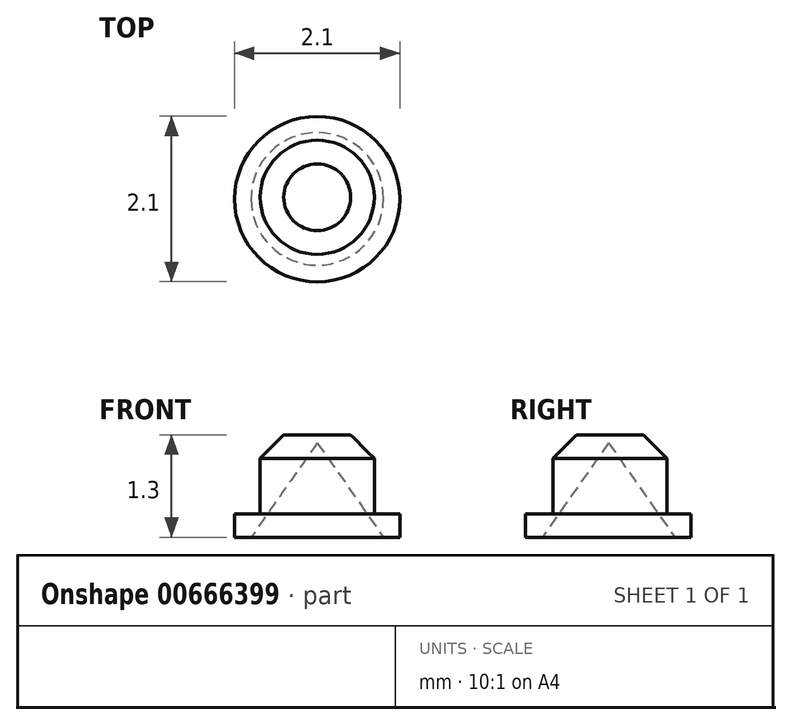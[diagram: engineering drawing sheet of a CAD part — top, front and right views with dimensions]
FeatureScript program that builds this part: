
annotation { "Feature Type Name" : "Feature", "Feature Type Description" : "" }
export const myFeature = defineFeature(function(context is Context, id is Id, definition is map)
    precondition{}
    {
        {
            var Q0;
            Q0=qCreatedBy(makeId("Top.planeOp"),FACE);
            var sketch = newSketch(context, id + "F0", { "sketchPlane" : qUnion([Q0])});
            skCircle(sketch, "E0", {"center": v(0, 0) * mm, "radius": 0.73 * mm});
            skSolve(sketch);
        }
        {
            var Q0;
            Q0=makeQuery(id+"F0.imprint","IMPRINT",FACE,{"disambiguationData":[TD([[makeQuery(id+"F0.imprint","IMPRINT",EDGE,{"derivedFrom":sQuery(id+"F0.wireOp",EDGE,"E0")}),1.0]])]});
            extrude(context, id + "F1", {"entities" : qUnion([Q0]), "flatOperationType" : FlatOperationType.REMOVE, "thickness1" : 5 * mm, "thickness2" : 0 * mm, "thickness" : 5 * mm, "depth" : 1 * mm, "offsetDistance" : 25 * mm, "startOffsetBound" : StartOffsetType.BLIND, "startOffsetDistance" : 25 * mm, "domain" : OperationDomain.MODEL});
        }
        {
            var Q0;
            Q0=makeQuery(id+"F1.opExtrude","CAP_FACE",FACE,{"disambiguationData":[OSD([sQuery(id+"F0.wireOp",EDGE,"E0")])],"isStart":true});
            var sketch = newSketch(context, id + "F2", { "sketchPlane" : qUnion([Q0])});
            skCircle(sketch, "E1", {"center": v(0, 0.02) * mm, "radius": 1.05 * mm});
            skSolve(sketch);
        }
        {
            var Q0;
            Q0=makeQuery(id+"F2.imprint","IMPRINT",FACE,{"disambiguationData":[TD([[makeQuery(id+"F2.imprint","IMPRINT",EDGE,{"derivedFrom":sQuery(id+"F2.wireOp",EDGE,"E1")}),1.0]])]});
            extrude(context, id + "F3", {"entities" : qUnion([Q0]), "operationType" : NewBodyOperationType.ADD, "depth" : -0.3 * mm, "offsetDistance" : 25 * mm});
        }
        {
            var Q0;
            Q0=makeQuery(id+"F1.opExtrude","CAP_FACE",FACE,{"disambiguationData":[OSD([sQuery(id+"F0.wireOp",EDGE,"E0")])],"isStart":false});
            extrude(context, id + "F4", {"entities" : qUnion([Q0]), "operationType" : NewBodyOperationType.ADD, "depth" : 0.3 * mm, "offsetDistance" : 25 * mm});
        }
        {
            var Q0;
            Q0=makeQuery(id+"F4.opExtrude","CAP_EDGE",EDGE,{"disambiguationData":[OSD([sQuery(id+"F0.wireOp",EDGE,"E0")])],"isStart":false});
            chamfer(context, id + "F5", {"entities" : qUnion([Q0]), "width" : 0.3 * mm, "tangentPropagation" : true});
        }
        {
            var Q0;
            Q0=qCreatedBy(makeId("Front.planeOp"),FACE);
            var sketch = newSketch(context, id + "F6", { "sketchPlane" : qUnion([Q0])});
            skLineSegment(sketch, "E2", {"start": v(0, 0) * mm, "end": v(0, -1.21) * mm});
            skLineSegment(sketch, "E3", {"start": v(0, -1.21) * mm, "end": v(-0.85, -1.21) * mm});
            skLineSegment(sketch, "E4", {"start": v(-0.85, -1.21) * mm, "end": v(0, 0) * mm});
            skSolve(sketch);
        }
        {
            var Q0;
            Q0=makeQuery(id+"F6.imprint","IMPRINT",FACE,{"disambiguationData":[TD([[makeQuery(id+"F6.imprint","IMPRINT",EDGE,{"derivedFrom":sQuery(id+"F6.wireOp",EDGE,"E2")}),-1.0]])]});
            var Q1;
            Q1=sQuery(id+"F6.wireOp",EDGE,"E2");
            revolve(context, id + "F7", {"entities" : qUnion([Q0]), "axis" : qUnion([Q1]), "revolveType" : RevolveType.FULL});
        }
        {
            var Q0;
            Q0=makeQuery(id+"F7.opRevolve","SWEPT_BODY",BODY,{"disambiguationData":[OSD([sQuery(id+"F6.wireOp",EDGE,"E2"),sQuery(id+"F6.wireOp",EDGE,"E3"),sQuery(id+"F6.wireOp",EDGE,"E4")])]});
            var Q1;
            Q1=qCreatedBy(makeId("Origin.pointOp"),VERTEX);
            transform(context, id + "F8", {"entities" : qUnion([Q0]), "transformType" : TransformType.TRANSLATION_3D, "dx" : 0 * mm, "dy" : 0 * mm, "dz" : 1 * mm, "makeCopy" : false});
        }
        {
            var Q0;
            Q0=makeQuery(id+"F7.opRevolve","SWEPT_BODY",BODY,{"disambiguationData":[OSD([sQuery(id+"F6.wireOp",EDGE,"E2"),sQuery(id+"F6.wireOp",EDGE,"E3"),sQuery(id+"F6.wireOp",EDGE,"E4")])]});
            transform(context, id + "F9", {"entities" : qUnion([Q0]), "transformType" : TransformType.TRANSLATION_3D, "dx" : 0 * mm, "dy" : 0 * mm, "dz" : 0.2 * mm, "makeCopy" : false});
        }
        {
            var Q0;
            Q0=makeQuery(id+"F7.opRevolve","SWEPT_BODY",BODY,{"disambiguationData":[OSD([sQuery(id+"F6.wireOp",EDGE,"E2"),sQuery(id+"F6.wireOp",EDGE,"E3"),sQuery(id+"F6.wireOp",EDGE,"E4")])]});
            transform(context, id + "F10", {"entities" : qUnion([Q0]), "transformType" : TransformType.TRANSLATION_3D, "dx" : 0 * mm, "dy" : -0.02 * mm, "dz" : 0 * mm, "makeCopy" : false});
        }
        {
            var Q0;
            Q0=makeQuery(id+"F7.opRevolve","SWEPT_BODY",BODY,{"disambiguationData":[OSD([sQuery(id+"F6.wireOp",EDGE,"E2"),sQuery(id+"F6.wireOp",EDGE,"E3"),sQuery(id+"F6.wireOp",EDGE,"E4")])]});
            var Q1;
            Q1=makeQuery(id+"F1.opExtrude","SWEPT_BODY",BODY,{"disambiguationData":[OSD([sQuery(id+"F0.wireOp",EDGE,"E0")])]});
            booleanBodies(context, id + "F11", {"operationType" : BooleanOperationType.SUBTRACTION, "tools" : qUnion([Q0]), "targets" : qUnion([Q1])});
        }
    });
